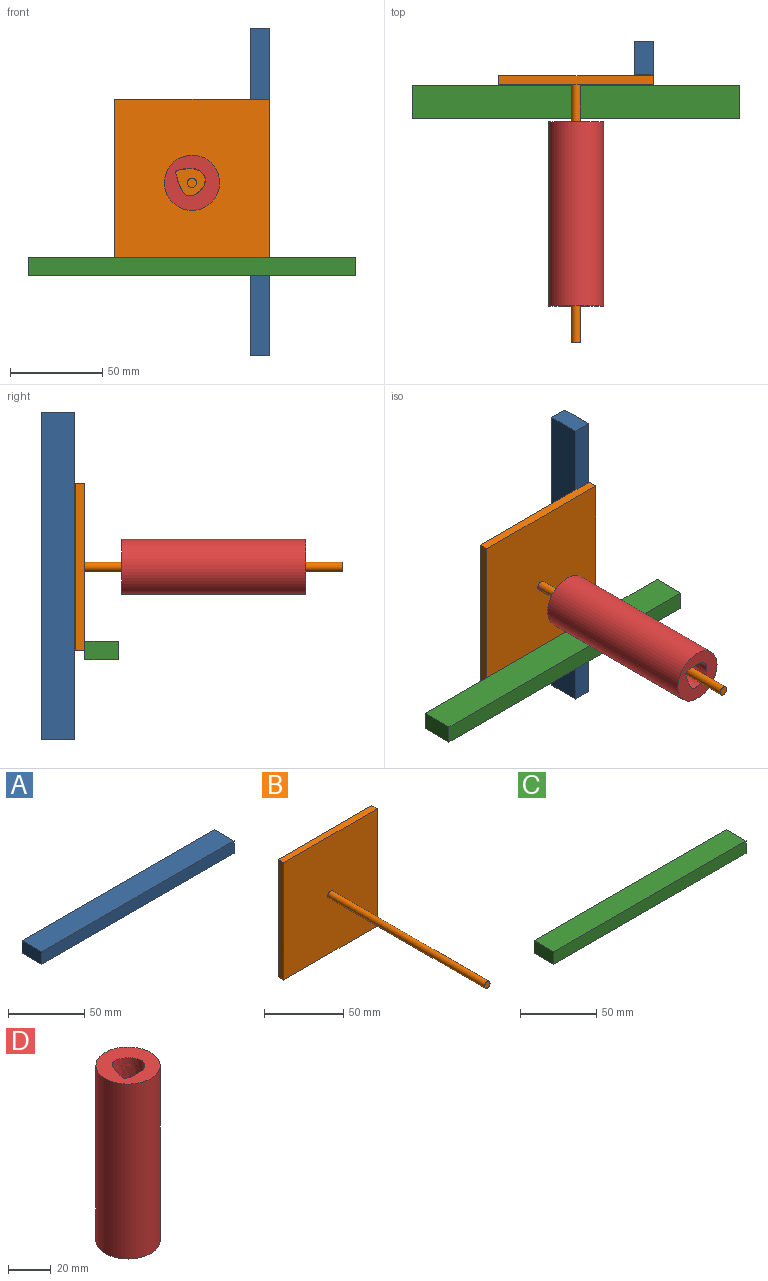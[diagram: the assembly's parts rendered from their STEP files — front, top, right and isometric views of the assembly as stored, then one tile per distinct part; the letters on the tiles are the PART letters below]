
ASSEMBLY  parts=4 mates=3
PART A: 6 faces, bbox 178x18.2x10 mm
  f0: plane 18.25x10mm, normal (1,0,0), area 182.5mm2, adj f1,f3,f4,f5
  f1: plane 177.99x10mm, normal (0,1,0), area 1779.9mm2, adj f0,f2,f4,f5
  f2: plane 18.25x10mm, normal (-1,0,0), area 182.5mm2, adj f1,f3,f4,f5
  f3: plane 177.99x10mm, normal (0,-1,0), area 1779.9mm2, adj f0,f2,f4,f5
  f4: plane 177.99x18.25mm, normal (0,0,1), area 3248.2mm2, adj f0,f1,f2,f3
  f5: plane 177.99x18.25mm, normal (0,0,-1), area 3248.2mm2, adj f0,f1,f2,f3
PART B: 8 faces, bbox 83.7x145x90.7 mm
  f0: plane 90.68x5mm, normal (1,0,0), area 453.4mm2, adj f1,f3,f4,f5
  f1: plane 83.66x5mm, normal (0,0,1), area 418.3mm2, adj f0,f2,f4,f5
  f2: plane 90.68x5mm, normal (-1,0,0), area 453.4mm2, adj f1,f3,f4,f5
  f3: plane 83.66x5mm, normal (0,0,-1), area 418.3mm2, adj f0,f2,f4,f5
  f4: plane 90.68x83.66mm, normal (0,-1,0), area 7567.1mm2, adj f0,f1,f2,f3,f6
  f5: plane 90.68x83.66mm, normal (0,1,0), area 7586.7mm2, adj f0,f1,f2,f3
  f6: cylinder r=2.5mm len=140mm, axis (0,1,0), area 2199.1mm2, adj f4,f7
  f7: plane 5x5mm, normal (0,-1,0), area 19.6mm2, adj f6
PART C: 6 faces, bbox 178x18.2x10 mm
  f0: plane 18.25x10mm, normal (1,0,0), area 182.5mm2, adj f1,f3,f4,f5
  f1: plane 177.99x10mm, normal (0,1,0), area 1779.9mm2, adj f0,f2,f4,f5
  f2: plane 18.25x10mm, normal (-1,0,0), area 182.5mm2, adj f1,f3,f4,f5
  f3: plane 177.99x10mm, normal (0,-1,0), area 1779.9mm2, adj f0,f2,f4,f5
  f4: plane 177.99x18.25mm, normal (0,0,1), area 3248.2mm2, adj f0,f1,f2,f3
  f5: plane 177.99x18.25mm, normal (0,0,-1), area 3248.2mm2, adj f0,f1,f2,f3
PART D: 4 faces, bbox 30x30x100 mm
  f0: plane 30x30mm, normal (0,0,1), area 524.2mm2, adj f2,f3
  f1: plane 30x30mm, normal (0,0,-1), area 524.2mm2, adj f2,f3
  f2: cylinder r=15mm len=100mm, axis (0,0,-1), area 9424.8mm2, adj f0,f1
  f3: extruded ~100x16.15mm, area 4947.5mm2, adj f0,f1
PLACE A rot(axis=(0,1,0),90deg) t=(56.96,113.69,26.89)mm
PLACE B t=(25.16,104.19,31.89)mm fixed
PLACE C t=(25.46,59.76,-18.45)mm
PLACE D rot(axis=(-1,0,0),90deg) t=(25.16,-20.81,31.89)mm
MATE slider A.f4 <-> B.f0  axis (1,0,0) through (66.96,113.69,26.89)mm
MATE slider B.f4 <-> C.f1  axis (0,-1,0) through (25.16,99.19,-13.45)mm
MATE revolute B.f6 <-> D.f2  axis (0,1,0) through (25.16,29.19,31.89)mm
